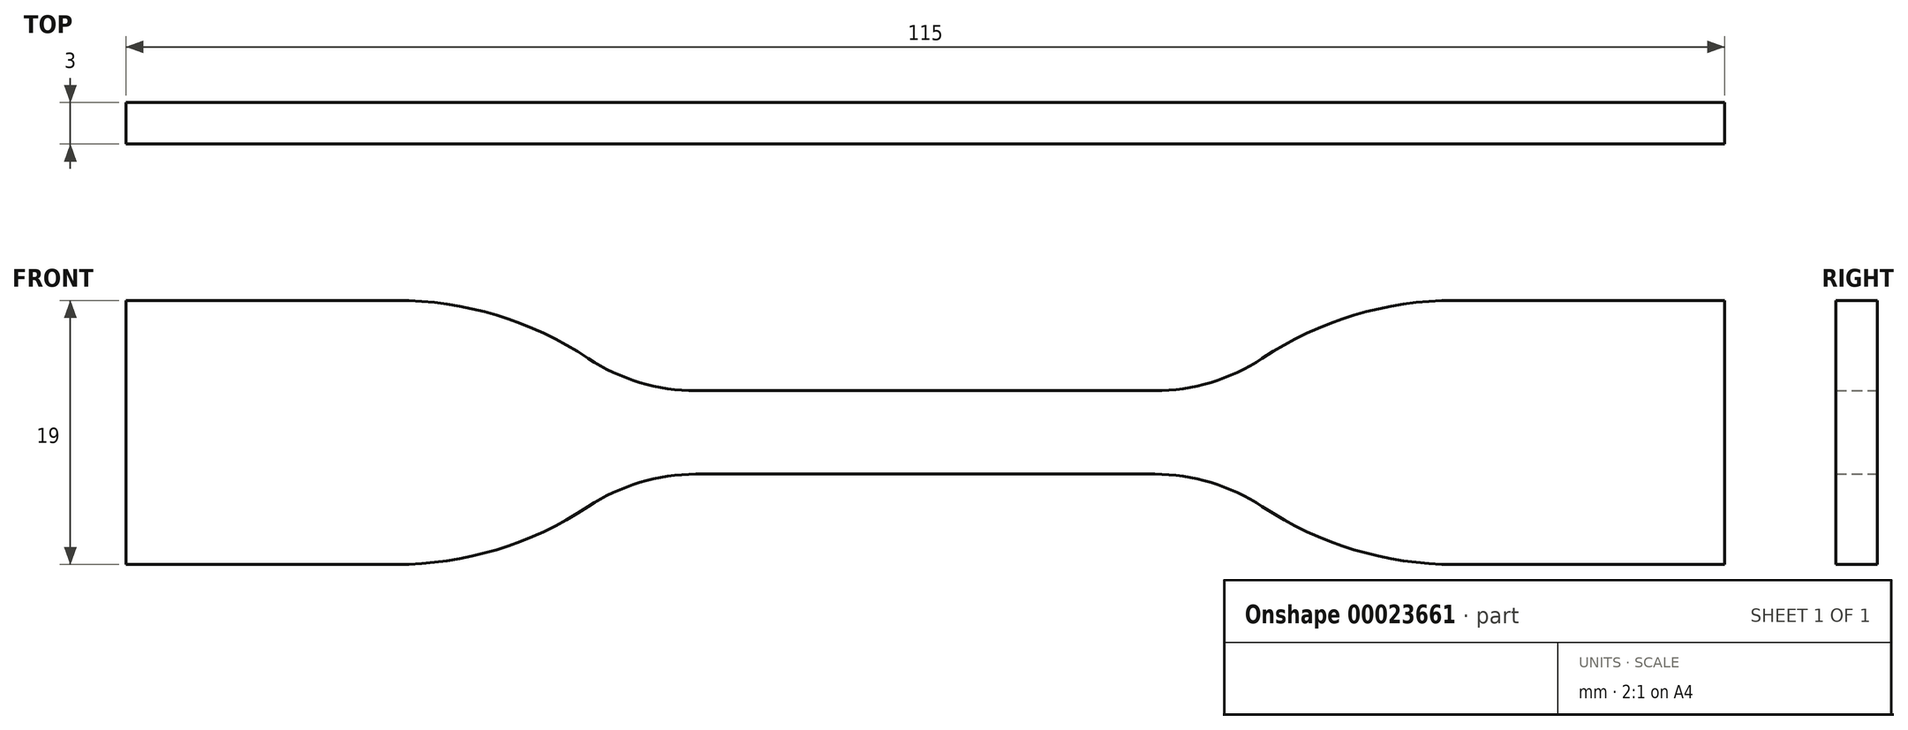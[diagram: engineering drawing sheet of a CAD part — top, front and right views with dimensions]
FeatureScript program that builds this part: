
annotation { "Feature Type Name" : "Feature", "Feature Type Description" : "" }
export const myFeature = defineFeature(function(context is Context, id is Id, definition is map)
    precondition{}
    {
        {
            var Q0;
            Q0=qCreatedBy(makeId("Front.planeOp"),FACE);
            var sketch = newSketch(context, id + "F0", { "sketchPlane" : qUnion([Q0])});
            skLineSegment(sketch, "E0", {"start": v(0, 3) * mm, "end": v(16.5, 3) * mm});
            skLineSegment(sketch, "E1", {"start": v(0, -3) * mm, "end": v(16.5, -3) * mm});
            skLineSegment(sketch, "E2", {"start": v(57.5, 9.5) * mm, "end": v(57.5, -9.5) * mm});
            skLineSegment(sketch, "E3", {"start": v(57.5, -9.5) * mm, "end": v(38.06, -9.5) * mm});
            skLineSegment(sketch, "E4", {"start": v(57.5, 9.5) * mm, "end": v(38.06, 9.5) * mm});
            skPoint(sketch, "E5", {"position": v(57.5, 0) * mm});
            skLineSegment(sketch, "E6", {"start": v(0, 3) * mm, "end": v(0, -3) * mm, "construction": true});
            skArc(sketch, "E7", {"start": v(16.5, 3) * mm, "mid": v(20.54, 3.6) * mm, "end": v(24.24, 5.33) * mm});
            skArc(sketch, "E8", {"start": v(38.06, 9.5) * mm, "mid": v(30.84, 8.44) * mm, "end": v(24.24, 5.33) * mm});
            skArc(sketch, "E9", {"start": v(24.24, -5.33) * mm, "mid": v(20.54, -3.6) * mm, "end": v(16.5, -3) * mm});
            skArc(sketch, "E10", {"start": v(24.24, -5.33) * mm, "mid": v(30.84, -8.44) * mm, "end": v(38.06, -9.5) * mm});
            skLineSegment(sketch, "E11.MirrorCS", {"start": v(0, 3) * mm, "end": v(-16.5, 3) * mm});
            skLineSegment(sketch, "E12.MirrorCS", {"start": v(0, -3) * mm, "end": v(-16.5, -3) * mm});
            skLineSegment(sketch, "E13.MirrorCS", {"start": v(-57.5, 9.5) * mm, "end": v(-57.5, -9.5) * mm});
            skPoint(sketch, "E14.MirrorP", {"position": v(-57.5, 0) * mm});
            skLineSegment(sketch, "E15.MirrorCS", {"start": v(-57.5, 9.5) * mm, "end": v(-38.06, 9.5) * mm});
            skLineSegment(sketch, "E16.MirrorCS", {"start": v(-57.5, -9.5) * mm, "end": v(-38.06, -9.5) * mm});
            skArc(sketch, "E17.MirrorCS", {"start": v(-24.24, -5.33) * mm, "mid": v(-20.54, -3.6) * mm, "end": v(-16.5, -3) * mm});
            skArc(sketch, "E18.MirrorCS", {"start": v(-24.24, -5.33) * mm, "mid": v(-30.84, -8.44) * mm, "end": v(-38.06, -9.5) * mm});
            skArc(sketch, "E19.MirrorCS", {"start": v(-38.06, 9.5) * mm, "mid": v(-30.84, 8.44) * mm, "end": v(-24.24, 5.33) * mm});
            skArc(sketch, "E20.MirrorCS", {"start": v(-16.5, 3) * mm, "mid": v(-20.54, 3.6) * mm, "end": v(-24.24, 5.33) * mm});
            skSolve(sketch);
        }
        {
            var Q0;
            Q0 = qSketchRegion(id + "F0", true);
            extrude(context, id + "F1", {"entities" : qUnion([Q0]), "endBound" : BoundingType.SYMMETRIC, "depth" : 3 * mm});
        }
    });
